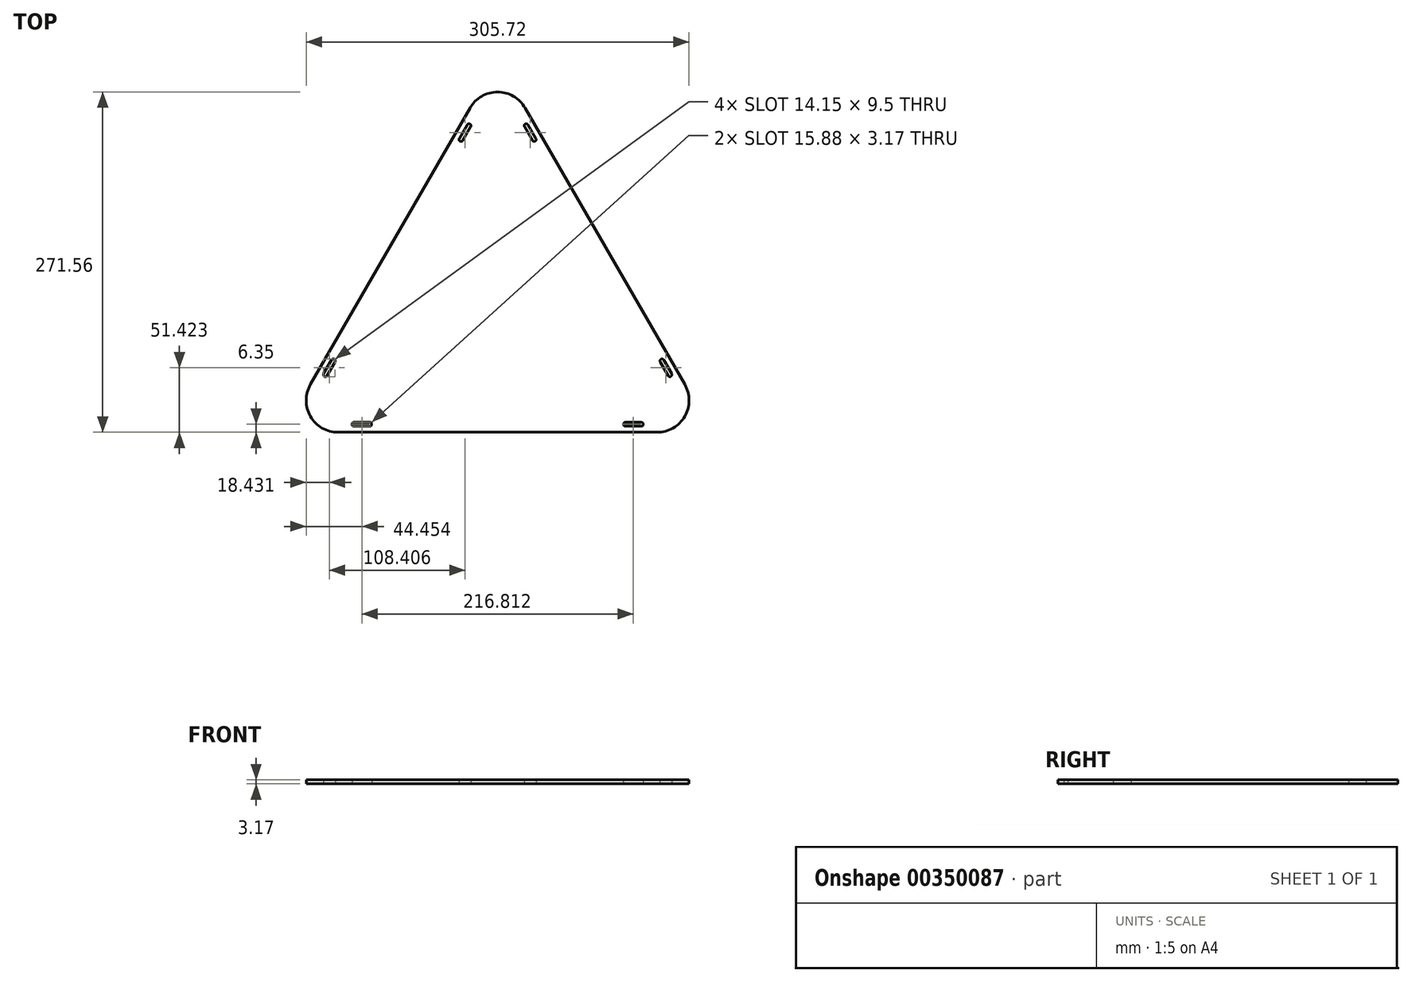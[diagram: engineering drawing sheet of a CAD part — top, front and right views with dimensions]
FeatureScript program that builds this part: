
annotation { "Feature Type Name" : "Feature", "Feature Type Description" : "" }
export const myFeature = defineFeature(function(context is Context, id is Id, definition is map)
    precondition{}
    {
        {
            var Q0;
            Q0=qCreatedBy(makeId("Top.planeOp"),FACE);
            var sketch = newSketch(context, id + "F0", { "sketchPlane" : qUnion([Q0])});
            skLineSegment(sketch, "E0", {"start": v(-127.46, 0) * mm, "end": v(127.46, 0) * mm});
            skLineSegment(sketch, "E1", {"start": v(-149.45, 38.1) * mm, "end": v(-22, 258.86) * mm});
            skLineSegment(sketch, "E2", {"start": v(149.45, 38.1) * mm, "end": v(22, 258.86) * mm});
            skPoint(sketch, "E3.visualSharp", {"position": v(-171.45, 0) * mm});
            skArc(sketch, "E3.filletArc", {"start": v(-149.45, 38.1) * mm, "mid": v(-149.45, 12.7) * mm, "end": v(-127.46, 0) * mm});
            skPoint(sketch, "E4.visualSharp", {"position": v(0, 296.96) * mm});
            skArc(sketch, "E4.filletArc", {"start": v(22, 258.86) * mm, "mid": v(0, 271.56) * mm, "end": v(-22, 258.86) * mm});
            skPoint(sketch, "E5.visualSharp", {"position": v(171.45, 0) * mm});
            skArc(sketch, "E5.filletArc", {"start": v(127.46, 0) * mm, "mid": v(149.45, 12.7) * mm, "end": v(149.45, 38.1) * mm});
            skLineSegment(sketch, "E6", {"start": v(-127.46, 0) * mm, "end": v(-127.46, 6.35) * mm, "construction": true});
            skLineSegment(sketch, "E7", {"start": v(-149.45, 38.1) * mm, "end": v(-143.95, 34.92) * mm, "construction": true});
            skLineSegment(sketch, "E8", {"start": v(127.46, 0) * mm, "end": v(127.46, 6.35) * mm, "construction": true});
            skLineSegment(sketch, "E9", {"start": v(149.45, 38.1) * mm, "end": v(143.95, 34.93) * mm, "construction": true});
            skLineSegment(sketch, "E10", {"start": v(22, 258.86) * mm, "end": v(16.5, 255.69) * mm, "construction": true});
            skLineSegment(sketch, "E11", {"start": v(-22, 258.86) * mm, "end": v(-16.5, 255.69) * mm, "construction": true});
            skLineSegment(sketch, "E12", {"start": v(-127.46, 6.35) * mm, "end": v(127.46, 6.35) * mm, "construction": true});
            skLineSegment(sketch, "E13", {"start": v(-16.5, 255.69) * mm, "end": v(-143.95, 34.92) * mm, "construction": true});
            skLineSegment(sketch, "E14", {"start": v(143.95, 34.92) * mm, "end": v(16.5, 255.69) * mm, "construction": true});
            skArc(sketch, "E15", {"start": v(-114.76, 7.94) * mm, "mid": v(-116.34, 6.35) * mm, "end": v(-114.76, 4.76) * mm});
            skArc(sketch, "E16", {"start": v(114.76, 4.76) * mm, "mid": v(116.34, 6.35) * mm, "end": v(114.76, 7.94) * mm});
            skArc(sketch, "E17", {"start": v(102.06, 7.94) * mm, "mid": v(100.47, 6.35) * mm, "end": v(102.06, 4.76) * mm});
            skArc(sketch, "E18", {"start": v(132.63, 57.72) * mm, "mid": v(130.46, 58.3) * mm, "end": v(129.88, 56.13) * mm});
            skArc(sketch, "E19", {"start": v(24.22, 245.48) * mm, "mid": v(22.05, 246.06) * mm, "end": v(21.47, 243.9) * mm});
            skArc(sketch, "E20", {"start": v(-21.47, 243.9) * mm, "mid": v(-22.05, 246.06) * mm, "end": v(-24.22, 245.48) * mm});
            skArc(sketch, "E21", {"start": v(-30.57, 234.48) * mm, "mid": v(-30, 232.31) * mm, "end": v(-27.82, 232.9) * mm});
            skArc(sketch, "E22", {"start": v(-138.98, 46.72) * mm, "mid": v(-138.4, 44.55) * mm, "end": v(-136.23, 45.13) * mm});
            skArc(sketch, "E23", {"start": v(-129.88, 56.13) * mm, "mid": v(-130.46, 58.3) * mm, "end": v(-132.63, 57.72) * mm});
            skArc(sketch, "E24", {"start": v(-102.06, 4.76) * mm, "mid": v(-100.47, 6.35) * mm, "end": v(-102.06, 7.94) * mm});
            skArc(sketch, "E25", {"start": v(136.23, 45.13) * mm, "mid": v(138.4, 44.55) * mm, "end": v(138.98, 46.72) * mm});
            skArc(sketch, "E26", {"start": v(27.82, 232.9) * mm, "mid": v(30, 232.31) * mm, "end": v(30.57, 234.48) * mm});
            skLineSegment(sketch, "E27", {"start": v(-114.76, 7.94) * mm, "end": v(-102.06, 7.94) * mm});
            skLineSegment(sketch, "E28", {"start": v(-102.06, 4.76) * mm, "end": v(-114.76, 4.76) * mm});
            skLineSegment(sketch, "E29", {"start": v(-138.98, 46.72) * mm, "end": v(-132.63, 57.72) * mm});
            skLineSegment(sketch, "E30", {"start": v(-129.88, 56.13) * mm, "end": v(-136.23, 45.13) * mm});
            skLineSegment(sketch, "E31", {"start": v(-21.47, 243.9) * mm, "end": v(-27.82, 232.9) * mm});
            skLineSegment(sketch, "E32", {"start": v(-24.22, 245.48) * mm, "end": v(-30.57, 234.48) * mm});
            skLineSegment(sketch, "E33", {"start": v(24.22, 245.48) * mm, "end": v(30.57, 234.48) * mm});
            skLineSegment(sketch, "E34", {"start": v(21.47, 243.9) * mm, "end": v(27.82, 232.9) * mm});
            skLineSegment(sketch, "E35", {"start": v(129.88, 56.13) * mm, "end": v(136.23, 45.13) * mm});
            skLineSegment(sketch, "E36", {"start": v(132.63, 57.72) * mm, "end": v(138.98, 46.72) * mm});
            skLineSegment(sketch, "E37", {"start": v(102.06, 4.76) * mm, "end": v(114.76, 4.76) * mm});
            skLineSegment(sketch, "E38", {"start": v(102.06, 7.94) * mm, "end": v(114.76, 7.94) * mm});
            skSolve(sketch);
        }
        {
            var Q0;
            Q0=makeQuery(id+"F0.imprint","IMPRINT",FACE,{"disambiguationData":[TD([[makeQuery(id+"F0.imprint","IMPRINT",EDGE,{"derivedFrom":sQuery(id+"F0.wireOp",EDGE,"E0")}),1.0]])]});
            extrude(context, id + "F1", {"entities" : qUnion([Q0]), "depth" : 3.17 * mm});
        }
    });
